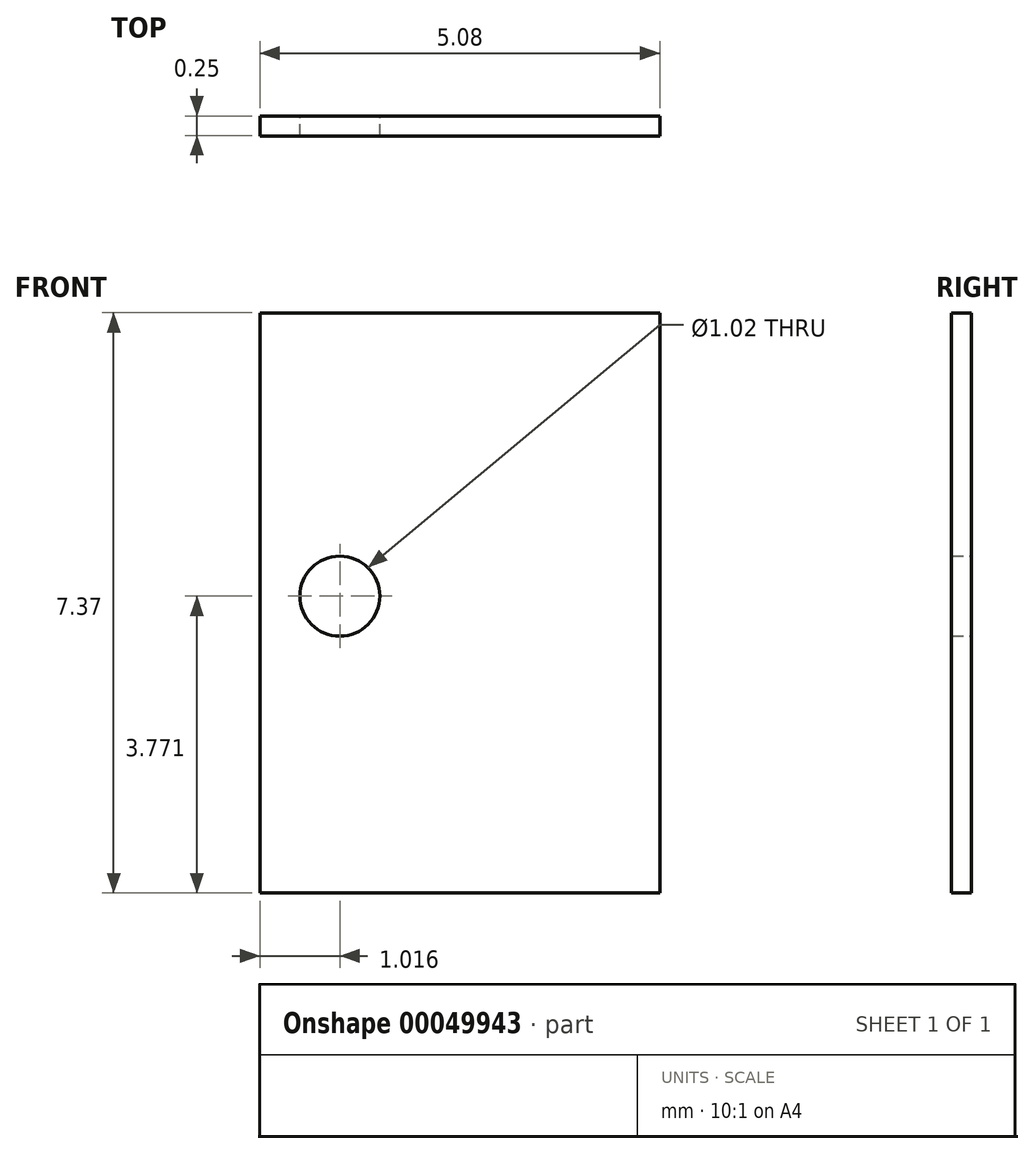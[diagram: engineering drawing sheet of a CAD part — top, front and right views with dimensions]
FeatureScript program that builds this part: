
annotation { "Feature Type Name" : "Feature", "Feature Type Description" : "" }
export const myFeature = defineFeature(function(context is Context, id is Id, definition is map)
    precondition{}
    {
        {
            var Q0;
            Q0=qCreatedBy(makeId("Front.planeOp"),FACE);
            var sketch = newSketch(context, id + "F0", { "sketchPlane" : qUnion([Q0])});
            skLineSegment(sketch, "E0", {"start": v(0, 0) * mm, "end": v(5.08, 0) * mm});
            skLineSegment(sketch, "E1", {"start": v(5.08, 0) * mm, "end": v(5.08, 7.37) * mm});
            skLineSegment(sketch, "E2", {"start": v(5.08, 7.37) * mm, "end": v(0, 7.37) * mm});
            skLineSegment(sketch, "E3", {"start": v(0, 7.37) * mm, "end": v(0, 0) * mm});
            skLineSegment(sketch, "E4", {"start": v(0, 3.77) * mm, "end": v(1.02, 3.77) * mm, "construction": true});
            skLineSegment(sketch, "E5", {"start": v(1.02, 3.77) * mm, "end": v(1.52, 3.77) * mm});
            skLineSegment(sketch, "E6", {"start": v(1.02, 3.77) * mm, "end": v(0.5, 3.77) * mm});
            skCircle(sketch, "E7", {"center": v(1.02, 3.77) * mm, "radius": 0.5 * mm});
            skSolve(sketch);
        }
        {
            var Q0;
            Q0 = qSketchRegion(id + "F0", true);
            extrude(context, id + "F1", {"entities" : qUnion([Q0]), "depth" : 0.25 * mm});
        }
    });
